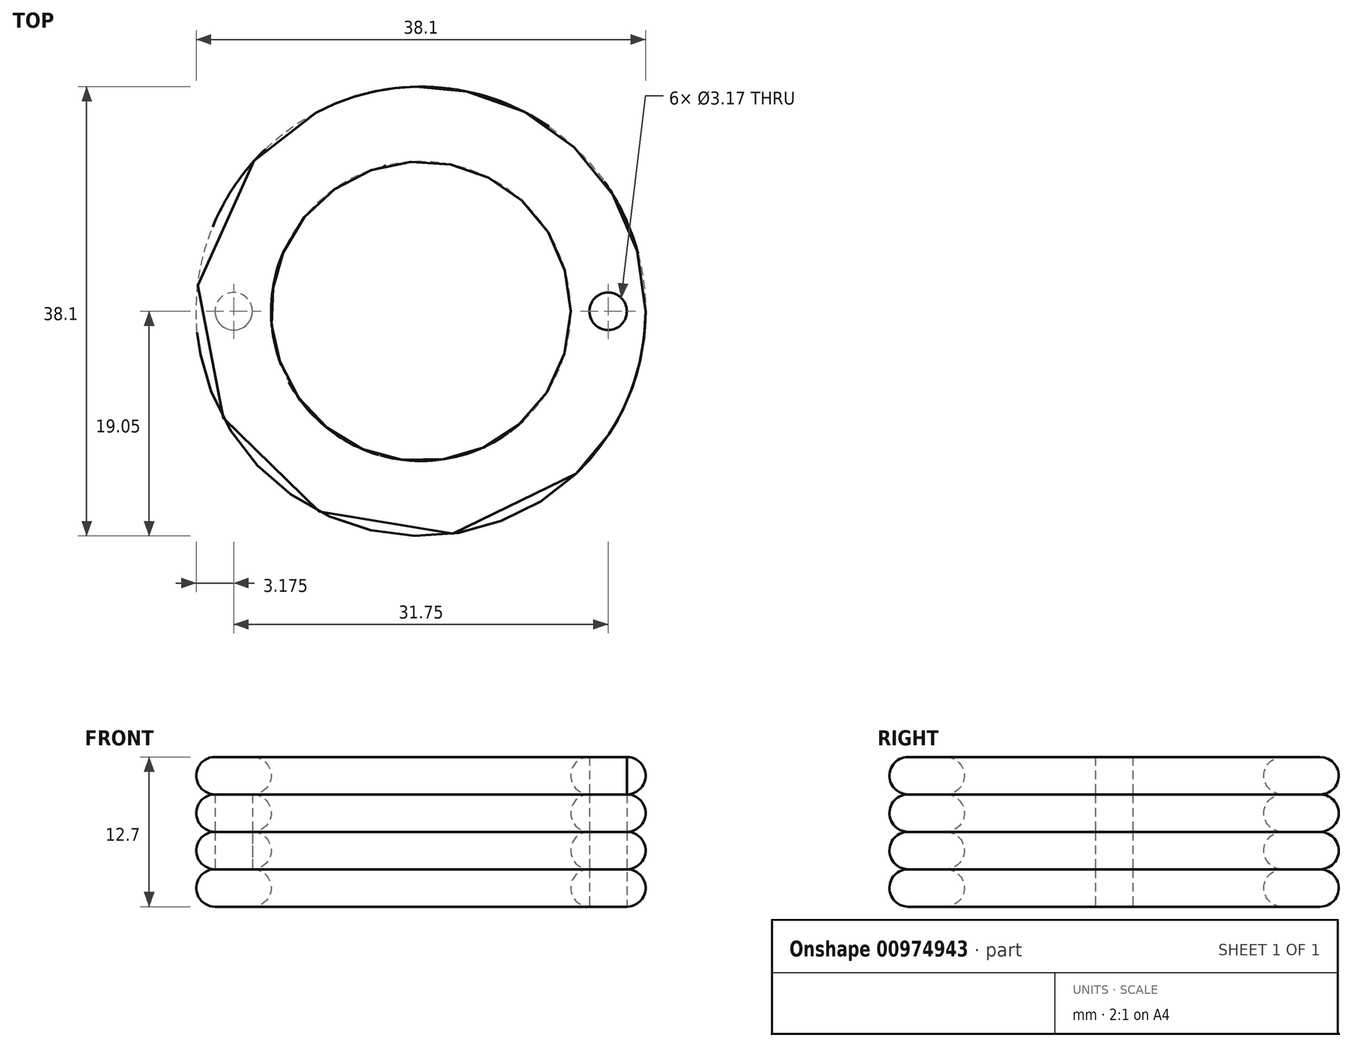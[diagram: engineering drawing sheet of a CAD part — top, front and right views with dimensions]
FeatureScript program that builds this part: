
annotation { "Feature Type Name" : "Feature", "Feature Type Description" : "" }
export const myFeature = defineFeature(function(context is Context, id is Id, definition is map)
    precondition{}
    {
        {
            var Q0;
            Q0=qCreatedBy(makeId("Top.planeOp"),FACE);
            var sketch = newSketch(context, id + "F0", { "sketchPlane" : qUnion([Q0])});
            skCircle(sketch, "E0", {"center": v(0, 0) * mm, "radius": 12.7 * mm});
            skCircle(sketch, "E1", {"center": v(0, 0) * mm, "radius": 19.05 * mm});
            skCircle(sketch, "E2", {"center": v(15.88, 0) * mm, "radius": 1.59 * mm});
            skCircle(sketch, "E3", {"center": v(-15.88, 0) * mm, "radius": 1.59 * mm});
            skSolve(sketch);
        }
        {
            var Q0;
            Q0=makeQuery(id+"F0.imprint","IMPRINT",FACE,{"disambiguationData":[TD([[makeQuery(id+"F0.imprint","IMPRINT",EDGE,{"derivedFrom":sQuery(id+"F0.wireOp",EDGE,"E0")}),-1.0]])]});
            var Q1;
            Q1=makeQuery(id+"F0.imprint","IMPRINT",FACE,{"disambiguationData":[TD([[makeQuery(id+"F0.imprint","IMPRINT",EDGE,{"derivedFrom":sQuery(id+"F0.wireOp",EDGE,"E3")}),1.0]])]});
            extrude(context, id + "F1", {"entities" : qUnion([Q0, Q1]), "depth" : 3.17 * mm, "offsetDistance" : 25.4 * mm});
        }
        {
            var Q0;
            Q0=makeQuery(id+"F0.imprint","IMPRINT",FACE,{"disambiguationData":[TD([[makeQuery(id+"F0.imprint","IMPRINT",EDGE,{"derivedFrom":sQuery(id+"F0.wireOp",EDGE,"E2")}),1.0]])]});
            extrude(context, id + "F2", {"entities" : qUnion([Q0]), "depth" : 6.35 * mm, "offsetDistance" : 25.4 * mm});
        }
        {
            var Q0;
            Q0=makeQuery(id+"F0.imprint","IMPRINT",FACE,{"disambiguationData":[TD([[makeQuery(id+"F0.imprint","IMPRINT",EDGE,{"derivedFrom":sQuery(id+"F0.wireOp",EDGE,"E0")}),-1.0]])]});
            extrude(context, id + "F3", {"entities" : qUnion([Q0]), "depth" : 6.35 * mm, "offsetDistance" : 25.4 * mm, "hasSecondDirection" : true, "secondDirectionOppositeDirection" : false, "secondDirectionDepth" : 3.17 * mm});
        }
        {
            var Q0;
            Q0=makeQuery(id+"F0.imprint","IMPRINT",FACE,{"disambiguationData":[TD([[makeQuery(id+"F0.imprint","IMPRINT",EDGE,{"derivedFrom":sQuery(id+"F0.wireOp",EDGE,"E3")}),1.0]])]});
            extrude(context, id + "F4", {"entities" : qUnion([Q0]), "depth" : 9.52 * mm, "offsetDistance" : 25.4 * mm, "hasSecondDirection" : true, "secondDirectionOppositeDirection" : false, "secondDirectionDepth" : 3.17 * mm});
        }
        {
            var Q0;
            Q0=makeQuery(id+"F0.imprint","IMPRINT",FACE,{"disambiguationData":[TD([[makeQuery(id+"F0.imprint","IMPRINT",EDGE,{"derivedFrom":sQuery(id+"F0.wireOp",EDGE,"E0")}),-1.0]])]});
            extrude(context, id + "F5", {"entities" : qUnion([Q0]), "depth" : 9.52 * mm, "offsetDistance" : 25.4 * mm, "hasSecondDirection" : true, "secondDirectionOppositeDirection" : false, "secondDirectionDepth" : 6.35 * mm});
        }
        {
            var Q0;
            Q0=makeQuery(id+"F0.imprint","IMPRINT",FACE,{"disambiguationData":[TD([[makeQuery(id+"F0.imprint","IMPRINT",EDGE,{"derivedFrom":sQuery(id+"F0.wireOp",EDGE,"E2")}),1.0]])]});
            extrude(context, id + "F6", {"entities" : qUnion([Q0]), "depth" : 12.7 * mm, "offsetDistance" : 25.4 * mm, "hasSecondDirection" : true, "secondDirectionOppositeDirection" : false, "secondDirectionDepth" : 6.35 * mm});
        }
        {
            var Q0;
            Q0=makeQuery(id+"F0.imprint","IMPRINT",FACE,{"disambiguationData":[TD([[makeQuery(id+"F0.imprint","IMPRINT",EDGE,{"derivedFrom":sQuery(id+"F0.wireOp",EDGE,"E0")}),-1.0]])]});
            var Q1;
            Q1=makeQuery(id+"F0.imprint","IMPRINT",FACE,{"disambiguationData":[TD([[makeQuery(id+"F0.imprint","IMPRINT",EDGE,{"derivedFrom":sQuery(id+"F0.wireOp",EDGE,"E3")}),1.0]])]});
            extrude(context, id + "F7", {"entities" : qUnion([Q0, Q1]), "depth" : 12.7 * mm, "offsetDistance" : 25.4 * mm, "hasSecondDirection" : true, "secondDirectionOppositeDirection" : false, "secondDirectionDepth" : 9.52 * mm});
        }
        {
            var Q0;
            Q0=makeQuery(id+"F1.opExtrude","SWEPT_FACE",FACE,{"disambiguationData":[OSD([sQuery(id+"F0.wireOp",EDGE,"E1")])]});
            var Q1;
            Q1=makeQuery(id+"F1.opExtrude","SWEPT_FACE",FACE,{"disambiguationData":[OSD([sQuery(id+"F0.wireOp",EDGE,"E0")])]});
            var Q2;
            Q2=makeQuery(id+"F5.opExtrude","SWEPT_FACE",FACE,{"disambiguationData":[OSD([sQuery(id+"F0.wireOp",EDGE,"E1")])]});
            var Q3;
            Q3=makeQuery(id+"F7.opExtrude","SWEPT_FACE",FACE,{"disambiguationData":[OSD([sQuery(id+"F0.wireOp",EDGE,"E1")])]});
            var Q4;
            Q4=makeQuery(id+"F3.opExtrude","SWEPT_FACE",FACE,{"disambiguationData":[OSD([sQuery(id+"F0.wireOp",EDGE,"E1")])]});
            var Q5;
            Q5=makeQuery(id+"F3.opExtrude","SWEPT_FACE",FACE,{"disambiguationData":[OSD([sQuery(id+"F0.wireOp",EDGE,"E0")])]});
            var Q6;
            Q6=makeQuery(id+"F5.opExtrude","SWEPT_FACE",FACE,{"disambiguationData":[OSD([sQuery(id+"F0.wireOp",EDGE,"E0")])]});
            var Q7;
            Q7=makeQuery(id+"F7.opExtrude","SWEPT_FACE",FACE,{"disambiguationData":[OSD([sQuery(id+"F0.wireOp",EDGE,"E0")])]});
            fillet(context, id + "F8", {"entities" : qUnion([Q0, Q1, Q2, Q3, Q4, Q5, Q6, Q7]), "radius" : 1.59 * mm, "tangentPropagation" : true, "allowEdgeOverflow" : false});
        }
    });
